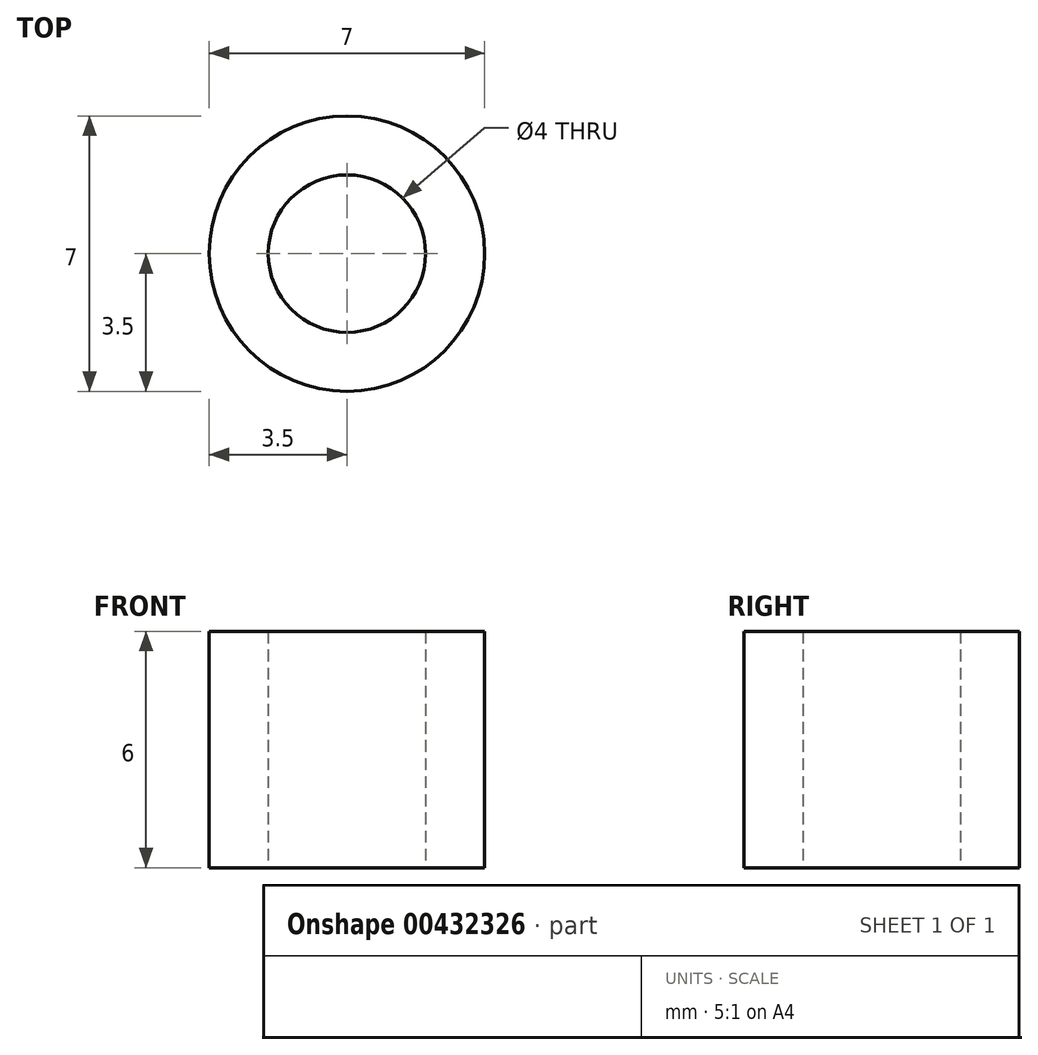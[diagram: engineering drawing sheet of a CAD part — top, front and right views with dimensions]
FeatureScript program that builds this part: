
annotation { "Feature Type Name" : "Feature", "Feature Type Description" : "" }
export const myFeature = defineFeature(function(context is Context, id is Id, definition is map)
    precondition{}
    {
        {
            var Q0;
            Q0=qCreatedBy(makeId("Top.planeOp"),FACE);
            var sketch = newSketch(context, id + "F0", { "sketchPlane" : qUnion([Q0])});
            skCircle(sketch, "E0", {"center": v(0, 0) * mm, "radius": 3.5 * mm});
            skCircle(sketch, "E1", {"center": v(0, 0) * mm, "radius": 2 * mm});
            skSolve(sketch);
        }
        {
            var Q0;
            Q0 = qSketchRegion(id + "F0", true);
            extrude(context, id + "F1", {"entities" : qUnion([Q0]), "depth" : 6 * mm});
        }
    });
